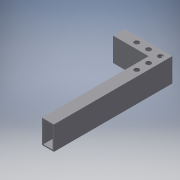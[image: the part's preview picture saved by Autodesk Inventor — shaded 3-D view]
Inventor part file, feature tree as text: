
AUTODESK INVENTOR PART (.ipt)
format: ipt  version: 2018 (Build 220112000, 112)  size: 162,816 bytes
history: native  units: in
note: dims shown in document units (in); Inventor stores cm internally (conversion verified against a paired STEP export)
features: extrude x4, sketch x4
ambient origin geometry x8: Origin, YZ Plane, XZ Plane, XY Plane, X Axis, Y Axis, Z Axis, Center Point
bodies: Body1 (feature_tree)
feature tree (8):
  extrude  "Extrusion12"  Depth=2.0in
  extrude  "Extrusion13"  Depth=0.1in
  extrude  "Extrusion14"  Depth=0.1in
  extrude  "Extrusion16"  Depth=1.0in
  sketch  "Sketch15"  dims[d46=1.0in d47=2.0in]
  sketch  "Sketch16"  dims[d48=0.1in d49=0.1in]
  sketch  "Sketch17"  dims[d50=0.1in d51=0.1in]
  sketch  "Sketch20"  dims[d52=3.0in d53=0.0in d54=1.0in d55=2.0in d56=0.1in d57=0.1in d58=0.1in d59=0.1in d60=10.0in d61=0.0in d62=0.1in d63=0.0in d71=0.5in d72=0.5in d73=0.5in d74=0.4167in d75=0.4167in d76=0.4167in d77=0.5in d78=0.5in d79=0.4167in d80=0.4167in d81=0.5in d82=1.0in d83=1.0in d84=1.0in d85=1.0in d86=3.0in d87=0.0in]
